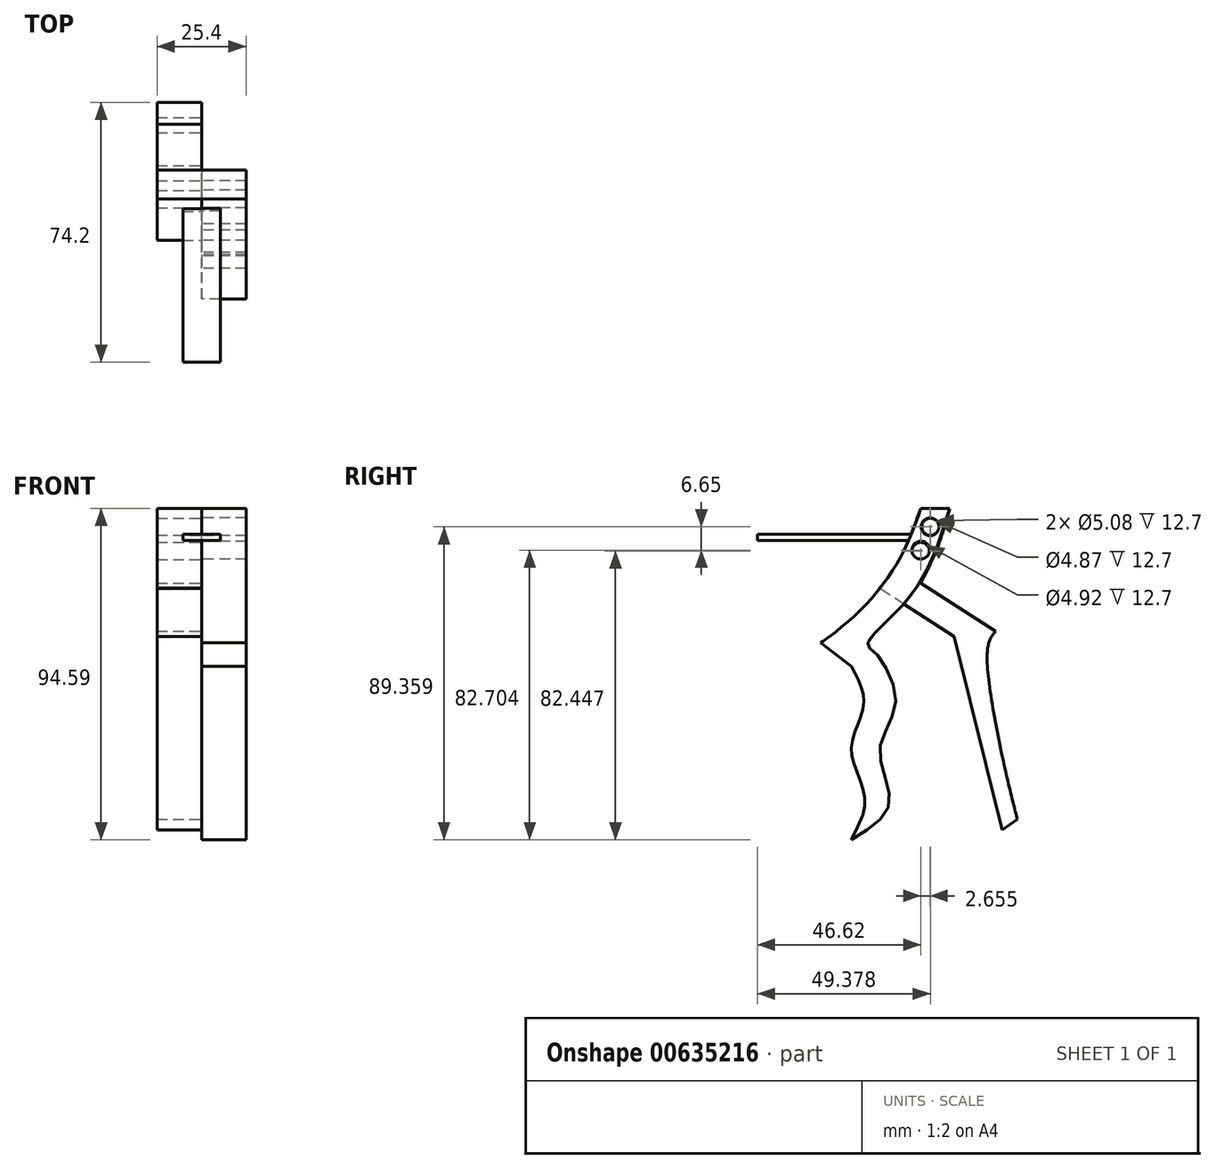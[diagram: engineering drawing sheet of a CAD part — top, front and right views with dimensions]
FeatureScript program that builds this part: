
annotation { "Feature Type Name" : "Feature", "Feature Type Description" : "" }
export const myFeature = defineFeature(function(context is Context, id is Id, definition is map)
    precondition{}
    {
        {
            var Q0;
            Q0=qCreatedBy(makeId("Right.planeOp"),FACE);
            var sketch = newSketch(context, id + "F0", { "sketchPlane" : qUnion([Q0])});
            skFitSpline(sketch, "E0", {"points": [v(0, 0) * mm, v(-6.8, -15.79) * mm, v(-20.71, -32.3) * mm, v(-28.53, -38.38) * mm, v(-28.82, -38.67) * mm], "startDerivative": vector(-16.62, -47.66) * mm, "endDerivative": vector(-3.54, -4.36) * mm});
            skFitSpline(sketch, "E1", {"points": [v(-28.53, -38.38) * mm, v(-19.84, -45.04) * mm], "startDerivative": vector(8.69, -6.66) * mm, "endDerivative": vector(8.69, -6.66) * mm});
            skFitSpline(sketch, "E2", {"points": [v(-19.84, -45.04) * mm, v(-16.26, -56.12) * mm, v(-19.84, -69.06) * mm, v(-15.91, -84.1) * mm, v(-19.84, -94.6) * mm, v(-19.84, -95.3) * mm], "startDerivative": vector(26.74, -48.47) * mm, "endDerivative": vector(3.18, -9.15) * mm});
            skFitSpline(sketch, "E3", {"points": [v(-19.84, -94.6) * mm, v(-8.92, -84.1) * mm, v(-11.72, -69.06) * mm, v(-7.17, -55.43) * mm, v(-13.11, -41.09) * mm, v(-15.21, -38.64) * mm, v(-2.97, -25) * mm, v(8.22, 0) * mm], "startDerivative": vector(105.76, 63.14) * mm, "endDerivative": vector(40.55, 134.55) * mm});
            skLineSegment(sketch, "E4", {"start": v(0, 0) * mm, "end": v(8.22, 0) * mm});
            skCircle(sketch, "E5", {"center": v(2.66, -5.24) * mm, "radius": 2.54 * mm});
            skCircle(sketch, "E6", {"center": v(0, -11.89) * mm, "radius": 2.54 * mm});
            skSolve(sketch);
        }
        {
            var Q0;
            Q0 = qSketchRegion(id + "F0", true);
            extrude(context, id + "F1", {"entities" : qUnion([Q0]), "depth" : 12.7 * mm, "offsetDistance" : 25.4 * mm});
        }
        {
            var Q0;
            Q0=qCreatedBy(makeId("Top.planeOp"),FACE);
            cPlane(context, id + "F2", {"entities" : qUnion([Q0]), "cplaneType" : CPlaneType.OFFSET, "offset" : 7.37 * mm, "oppositeDirection" : true, "width" : 152.4 * mm, "height" : 152.4 * mm});
        }
        {
            var Q0;
            Q0=qCreatedBy(id+"F2.planeOp",FACE);
            var sketch = newSketch(context, id + "F3", { "sketchPlane" : qUnion([Q0])});
            skLineSegment(sketch, "E7.bottom", {"start": v(5.33, 0) * mm, "end": v(-5.33, 0) * mm});
            skLineSegment(sketch, "E7.top", {"start": v(5.33, -46.62) * mm, "end": v(-5.33, -46.62) * mm});
            skLineSegment(sketch, "E7.left", {"start": v(5.33, 0) * mm, "end": v(5.33, -46.62) * mm});
            skLineSegment(sketch, "E7.right", {"start": v(-5.33, 0) * mm, "end": v(-5.33, -46.62) * mm});
            skPoint(sketch, "E7.middle", {"position": v(0, -23.3) * mm});
            skSolve(sketch);
        }
        {
            var Q0;
            Q0=makeQuery(id+"F3.imprint","IMPRINT",FACE,{"disambiguationData":[TD([[makeQuery(id+"F3.imprint","IMPRINT",EDGE,{"derivedFrom":sQuery(id+"F3.wireOp",EDGE,"E7.bottom")}),1.0]])]});
            extrude(context, id + "F4", {"entities" : qUnion([Q0]), "operationType" : NewBodyOperationType.ADD, "oppositeDirection" : true, "depth" : 1.78 * mm, "offsetDistance" : 25.4 * mm});
        }
        {
            var Q0;
            Q0=qCreatedBy(makeId("Right.planeOp"),FACE);
            var sketch = newSketch(context, id + "F5", { "sketchPlane" : qUnion([Q0])});
            skLineSegment(sketch, "E8", {"start": v(8.28, 0) * mm, "end": v(0, 0) * mm});
            skFitSpline(sketch, "E9", {"points": [v(8.28, 0) * mm, v(4.87, -10.92) * mm, v(0, -21.27) * mm], "startDerivative": vector(-6.1, -22.13) * mm, "endDerivative": vector(-10.47, -20.42) * mm});
            skFitSpline(sketch, "E10", {"points": [v(0, 0) * mm, v(-3.3, -8.59) * mm, v(-8.32, -18.27) * mm, v(-11.82, -22.86) * mm, v(-11.74, -22.78) * mm], "startDerivative": vector(-9.42, -25.4) * mm, "endDerivative": vector(3.26, 3.41) * mm});
            skLineSegment(sketch, "E11", {"start": v(21.37, -35.03) * mm, "end": v(0, -21.27) * mm});
            skLineSegment(sketch, "E12", {"start": v(9.51, -36.54) * mm, "end": v(-11.74, -22.78) * mm});
            skLineSegment(sketch, "E13", {"start": v(23.29, -91.8) * mm, "end": v(9.51, -36.54) * mm});
            skFitSpline(sketch, "E14", {"points": [v(21.37, -35.03) * mm, v(18.94, -43.33) * mm, v(28.56, -91.94) * mm, v(28.69, -92.07) * mm], "startDerivative": vector(-13.53, -16.16) * mm, "endDerivative": vector(2.52, -0.28) * mm});
            skLineSegment(sketch, "E15", {"start": v(28.66, -92.06) * mm, "end": v(23.29, -91.8) * mm});
            skLineSegment(sketch, "E16", {"start": v(18.94, -43.33) * mm, "end": v(9.51, -36.54) * mm});
            skLineSegment(sketch, "E17", {"start": v(18.94, -43.33) * mm, "end": v(11.66, -45.14) * mm});
            skLineSegment(sketch, "E18", {"start": v(23.18, -70.21) * mm, "end": v(18.22, -71.45) * mm});
            skLineSegment(sketch, "E19", {"start": v(27.58, -88.75) * mm, "end": v(23.29, -91.8) * mm});
            skCircle(sketch, "E20", {"center": v(2.76, -5.23) * mm, "radius": 2.44 * mm});
            skCircle(sketch, "E21", {"center": v(0, -12.14) * mm, "radius": 2.46 * mm});
            skSolve(sketch);
        }
        {
            var Q0;
            Q0=makeQuery(id+"F5.imprint","IMPRINT",FACE,{"disambiguationData":[TD([[makeQuery(id+"F5.imprint","IMPRINT",EDGE,{"derivedFrom":sQuery(id+"F5.wireOp",EDGE,"E8")}),1.0]])]});
            extrude(context, id + "F6", {"entities" : qUnion([Q0]), "operationType" : NewBodyOperationType.ADD, "oppositeDirection" : true, "depth" : 12.7 * mm, "offsetDistance" : 25.4 * mm});
        }
        {
            var Q0;
            Q0 = qSketchRegion(id + "F5", true);
            extrude(context, id + "F7", {"entities" : qUnion([Q0]), "operationType" : NewBodyOperationType.ADD, "oppositeDirection" : true, "depth" : 12.7 * mm, "offsetDistance" : 25.4 * mm});
        }
    });
